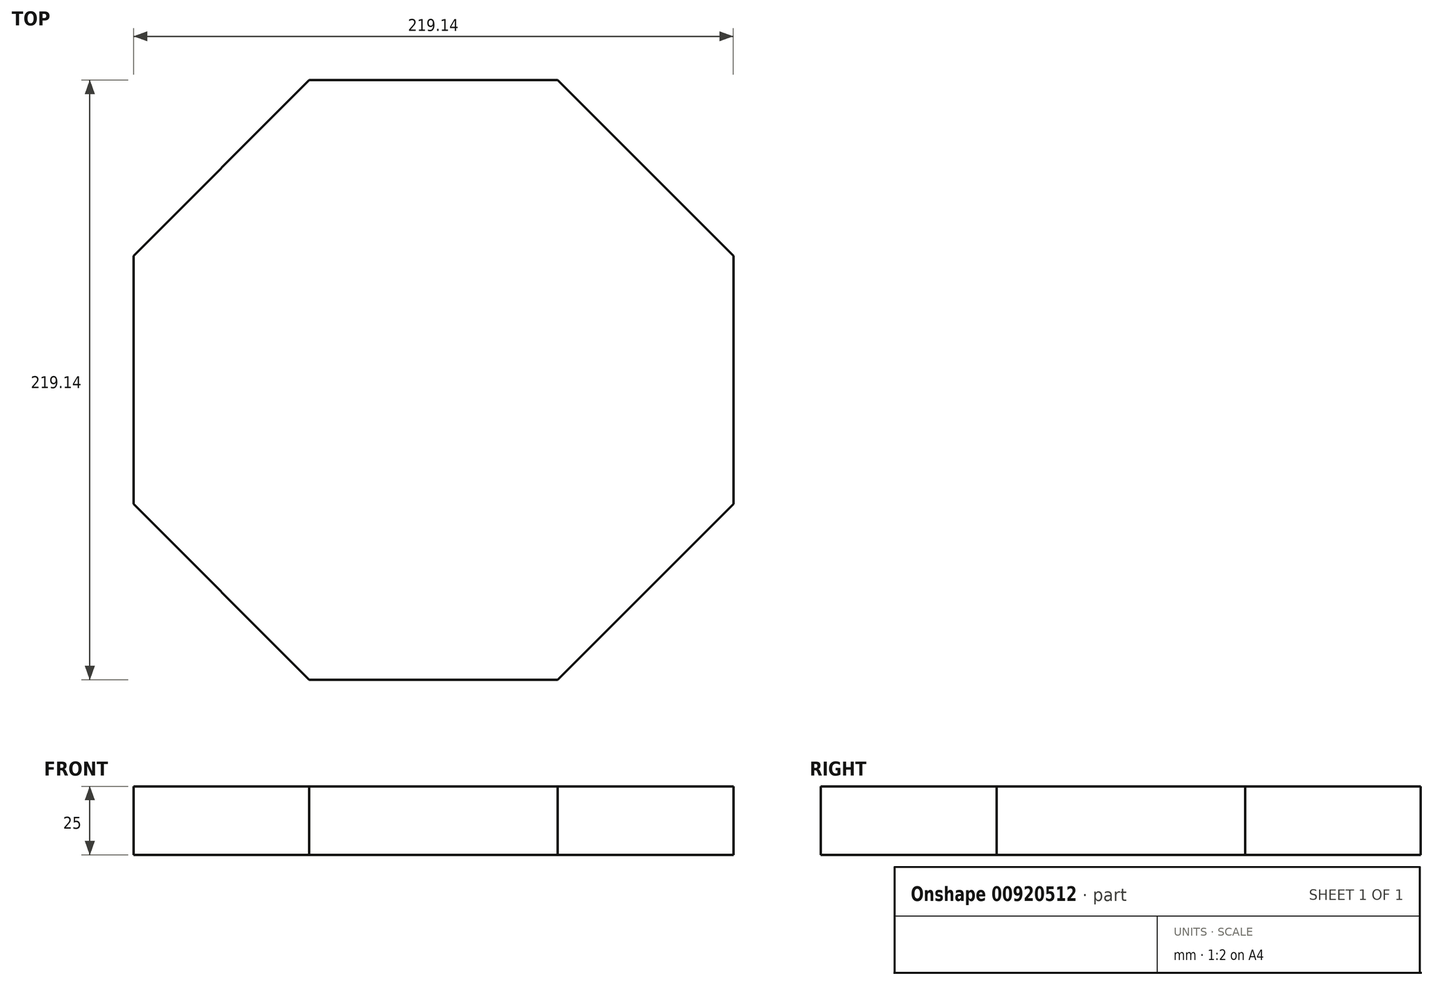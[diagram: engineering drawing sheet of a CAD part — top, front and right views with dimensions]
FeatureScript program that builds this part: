
annotation { "Feature Type Name" : "Feature", "Feature Type Description" : "" }
export const myFeature = defineFeature(function(context is Context, id is Id, definition is map)
    precondition{}
    {
        {
            var Q0;
            Q0=qCreatedBy(makeId("Top.planeOp"),FACE);
            var sketch = newSketch(context, id + "F0", { "sketchPlane" : qUnion([Q0])});
            skCircle(sketch, "E0.cCircle", {"center": v(0, 0) * mm, "radius": 109.57 * mm, "construction": true});
            skLineSegment(sketch, "E0.0", {"start": v(45.39, -109.57) * mm, "end": v(-45.39, -109.57) * mm});
            skLineSegment(sketch, "E0.1", {"start": v(-45.39, -109.57) * mm, "end": v(-109.57, -45.39) * mm});
            skLineSegment(sketch, "E0.2", {"start": v(-109.57, -45.39) * mm, "end": v(-109.57, 45.39) * mm});
            skLineSegment(sketch, "E0.3", {"start": v(-109.57, 45.39) * mm, "end": v(-45.39, 109.57) * mm});
            skLineSegment(sketch, "E0.4", {"start": v(-45.39, 109.57) * mm, "end": v(45.39, 109.57) * mm});
            skLineSegment(sketch, "E0.5", {"start": v(45.39, 109.57) * mm, "end": v(109.57, 45.39) * mm});
            skLineSegment(sketch, "E0.6", {"start": v(109.57, 45.39) * mm, "end": v(109.57, -45.39) * mm});
            skLineSegment(sketch, "E0.7", {"start": v(109.57, -45.39) * mm, "end": v(45.39, -109.57) * mm});
            skPoint(sketch, "E0.0.midPoint", {"position": v(0, -109.57) * mm});
            skSolve(sketch);
        }
        {
            var Q0;
            Q0 = qSketchRegion(id + "F0", true);
            extrude(context, id + "F1", {"entities" : qUnion([Q0]), "depth" : 25 * mm, "offsetDistance" : 25 * mm});
        }
    });
